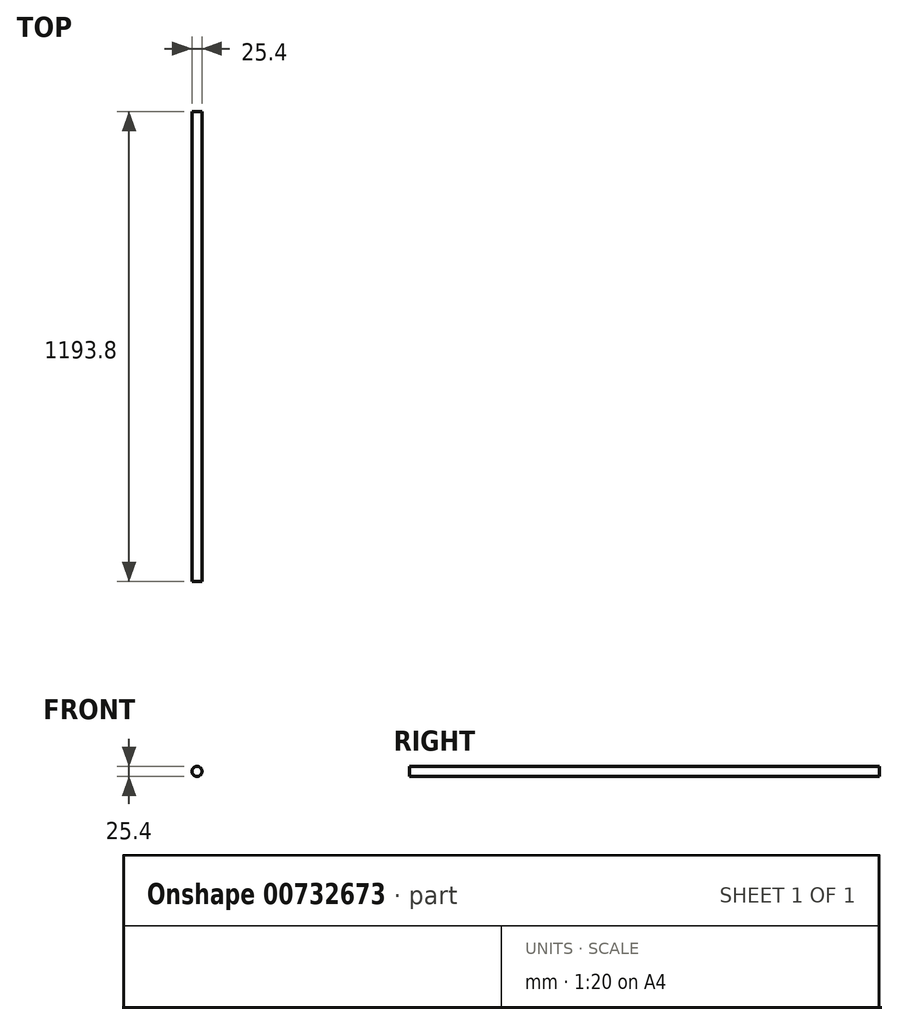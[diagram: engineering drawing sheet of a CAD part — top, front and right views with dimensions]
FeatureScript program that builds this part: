
annotation { "Feature Type Name" : "Feature", "Feature Type Description" : "" }
export const myFeature = defineFeature(function(context is Context, id is Id, definition is map)
    precondition{}
    {
        {
            var Q0;
            Q0=qCreatedBy(makeId("Front.planeOp"),FACE);
            var sketch = newSketch(context, id + "F0", { "sketchPlane" : qUnion([Q0])});
            skCircle(sketch, "E0", {"center": v(0, 0) * mm, "radius": 12.7 * mm});
            skSolve(sketch);
        }
        {
            var Q0;
            Q0 = qSketchRegion(id + "F0", true);
            extrude(context, id + "F1", {"entities" : qUnion([Q0]), "depth" : 1193.8 * mm, "offsetDistance" : 25.4 * mm});
        }
    });
